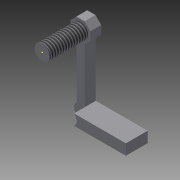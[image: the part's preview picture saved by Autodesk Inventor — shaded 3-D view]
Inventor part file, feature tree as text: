
AUTODESK INVENTOR PART (.ipt)
format: ipt  version: 2015 SP2 (Build 190223200, 223)  size: 118,272 bytes
history: native  units: mm
features: sketch x11, extrude x5, thread x1
ambient origin geometry x8: Origin, YZ Plane, XZ Plane, XY Plane, X Axis, Y Axis, Z Axis, Center Point
bodies: Solid1 (feature_tree)
feature tree (17):
  sketch  "Sketch1"  dims[d0=2.8mm d1=7.0mm d2=0.0mm]
  sketch  "Sketch2"  dims[d4=2.0mm d5=0.0mm d6=10.0mm d7=0.0mm]
  extrude  "Extrusion1"  Depth=7.0mm TaperAngle=0.0deg
  extrude  "Extrusion2"  Depth=10.0mm TaperAngle=0.0deg
  extrude  "Extrusion3"  Depth=2.0mm TaperAngle=0.0deg
  sketch  "Sketch5"
  sketch  "Sketch6"
  thread  "Thread1"  [1 undecoded]
  extrude  "Extrusion4"  [1 undecoded]
  sketch  "Sketch8"
  sketch  "Sketch9"
  extrude  "Extrusion5"  [1 undecoded]
  sketch  "Sketch11"
  sketch  "Sketch3"  dims[d8=10.0mm d9=0.0mm d10=2.0mm d11=0.0mm d12=4.0mm d13=0.0mm]
  sketch  "Sketch4"
  sketch  "Sketch7"
  sketch  "Sketch10"
note: 3 required parameter values undecoded (feature->parameter linkage not recoverable at this tier; creation-order binding heuristic only, values carry confidence <= 0.55)
